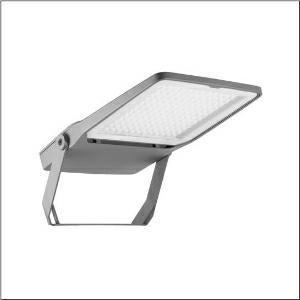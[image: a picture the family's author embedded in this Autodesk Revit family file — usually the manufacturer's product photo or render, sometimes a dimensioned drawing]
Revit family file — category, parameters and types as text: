
# Revit family: floodlight_fl_20_midi___pl43_5xa7682d3a1ac_4fa5
name_source: partatom
category: Lighting Fixtures
units: mm (PartAtom-declared; Revit-internal decimal feet)

## family parameters
Cut with Voids When Loaded = No
Host = Face
Light Source = No
Part Type = Normal
Room Calculation Point = No
Round Connector Dimension = Use Diameter
Shared = No

## types (1)
- --- (1 x LED 5000K / CRI = 70 (unbekannt), 19360 lm, 5000K)
    Apparent Load = 142 VA
    CIE Flux Codes = 32 74 99 100 100
    Color Rendering = 70
    Color Temperature = 5000K
    Default Elevation = 1800 mm
    Description = Floodlight FL 20 midi, floodlight, primary light control with lens, of plastic, primary optical cover: protective disc, of toughened safety glass, transparent, light distribution: PL43, light emission: direct distribution, primary light characteristic: asymmetric, installation type: surface-mounted, LED High Power LED, rated luminous flux: 19.360 lm, light colour: 750, colour temperature: 5000K, control gear: ECG Plus, control: flexible luminous flux parameterisation, time-dependent luminous flux control, digital communication interface, power reduction, overheat protection, electronic power reduction, with terminal, 5-pole, max. 2.5mm², mains connection: 220..240V, AC, 50/60Hz, rated input power: 142W, LED unit, of diecast aluminium, powder-coated, Siteco® metallic grey (DB 702S), length: 654 mm, width: 450 mm, height: 76mm, housing frame, of diecast aluminium, powder-coated, Siteco® metallic grey (DB 702S), mounting bracket, of steel, powder-coated, Siteco® metallic grey (DB 702S), DALIprotection rating (complete): IP66, insulation class (complete): insulation class II (safety insulation), certification: CE, ENEC, VDE, protection symbol: D, permissible ambient temperature for indoor applications: -40..+40°C, permissible ambient temperature for outdoor applications: -40..+50°C, standard: DIN EN 12944, packaging unit: 1 piece

Light Distribution: PL43
    Height = 76 mm
    Lamp = 1 x LED 5000K / CRI >= 70 (unbekannt)
    Lamp Light Flux = 19360 lm
    Lamp count = 1
    Length = 672 mm
    Luminous efficacy = 136 lm/W
    Manufacturer = Siteco
    ModVariant = No
    Model = 5XA7682D3A1AC
    Number of Poles = 1
    OnlyDefault = Yes
    Power Factor = 1
    Product Name = Floodlight FL 20 midi | PL43
    Product group = floodlight | pylon top
    ProductGroupID = 6101
    Protection Class = Protection class II
    Protection Degree = IP 66
    RLX_Detail_Level = 1
    RlxData = <blob elided: 97217 chars, md5=3ea38519>
    Socket = socket
    Standby Power = 0 W
    System Light Flux = 19360 lm
    System Power = 142 W
    Type Comments = factory setting: luminous flux: 100 % | dim-lin: 254 | 489 mA
    Type Image = l_1005943.jpg
    URL = http://relux.com
    VarID = @adj_143911
    Voltage = 0 V
    Weight = 0.00 kg
    Width = 450 mm

## geometry (parser evidence)
native form markers: Blend x4, Sweep x11
no freeform markers — native parametric forms only
